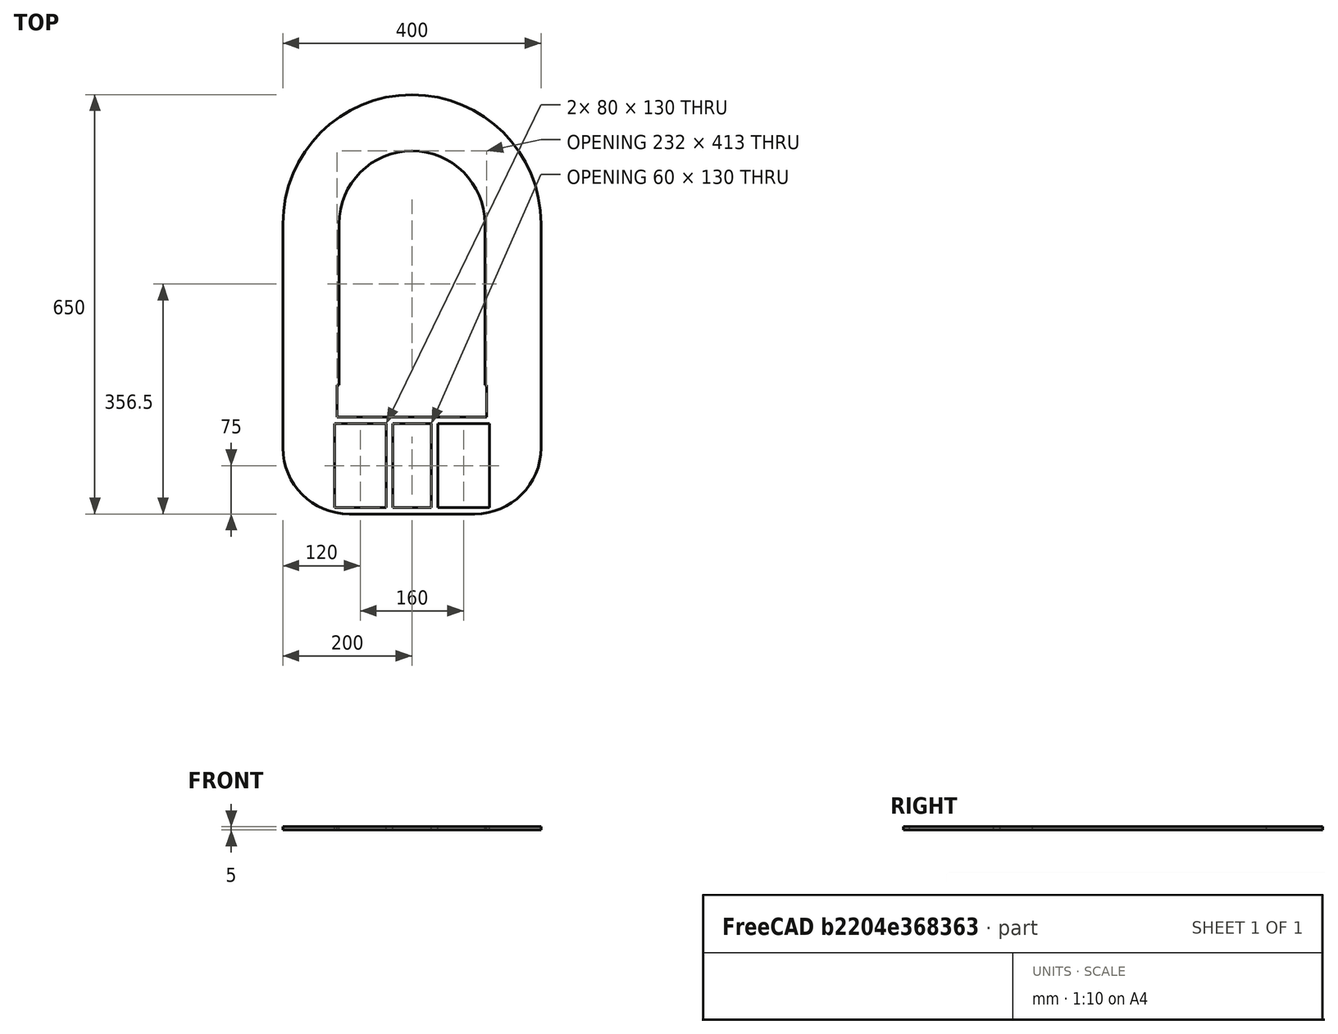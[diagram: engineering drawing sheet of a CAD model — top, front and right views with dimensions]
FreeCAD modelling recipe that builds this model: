
FCSTD DOCUMENT  (FreeCAD 0.16R6706 (Git))
Label: PlateauSuperieur
License: All rights reserved
LicenseURL: http://en.wikipedia.org/wiki/All_rights_reserved
objects: Sketcher::SketchObject×1, PartDesign::Pad×1
note: 3 computed .brp shape members not serialized (recipe doc carries the construction recipe); baked Part::Feature solids carry a one-line shape summary decoded from their .brp

FEATURE [Sketcher::SketchObject] Sketch
  sketch-geometry (32):
    g0: LineSegment StartX=0 StartY=-300 StartZ=0 EndX=116 EndY=-300 EndZ=0
    g1: LineSegment StartX=116 StartY=-300 StartZ=0 EndX=116 EndY=-250 EndZ=0
    g2: LineSegment StartX=116 StartY=-250 StartZ=0 EndX=113 EndY=-250 EndZ=0
    g3: LineSegment StartX=113 StartY=-250 StartZ=0 EndX=113 EndY=-0.000122513 EndZ=0
    g4: ArcOfCircle CenterX=0 CenterY=0 CenterZ=0 NormalX=0 NormalY=0 NormalZ=1 Radius=113 StartAngle=6.28318 EndAngle=7.85398
    g5: ArcOfCircle CenterX=0 CenterY=0 CenterZ=0 NormalX=0 NormalY=0 NormalZ=1 Radius=200 StartAngle=1.2861e-08 EndAngle=1.5708
    g6: LineSegment StartX=200 StartY=2.5722e-06 StartZ=0 EndX=200 EndY=-347.34 EndZ=0
    g7: LineSegment StartX=0 StartY=-450 StartZ=0 EndX=97.34 EndY=-450 EndZ=0
    g8: ArcOfCircle CenterX=97.34 CenterY=-347.34 CenterZ=0 NormalX=0 NormalY=0 NormalZ=1 Radius=102.66 StartAngle=4.71239 EndAngle=6.28319
    g9: LineSegment StartX=40 StartY=-310 StartZ=0 EndX=120 EndY=-310 EndZ=0
    g10: LineSegment StartX=120 StartY=-310 StartZ=0 EndX=120 EndY=-440 EndZ=0
    g11: LineSegment StartX=120 StartY=-440 StartZ=0 EndX=40 EndY=-440 EndZ=0
    g12: LineSegment StartX=40 StartY=-440 StartZ=0 EndX=40 EndY=-310 EndZ=0
    g13: LineSegment StartX=0 StartY=-310 StartZ=0 EndX=30 EndY=-310 EndZ=0
    g14: LineSegment StartX=30 StartY=-310 StartZ=0 EndX=30 EndY=-440 EndZ=0
    g15: LineSegment StartX=30 StartY=-440 StartZ=0 EndX=0 EndY=-440 EndZ=0
    g16: LineSegment StartX=0 StartY=-300 StartZ=0 EndX=-116 EndY=-300 EndZ=0
    g17: LineSegment StartX=-116 StartY=-300 StartZ=0 EndX=-116 EndY=-250 EndZ=0
    g18: LineSegment StartX=-116 StartY=-250 StartZ=0 EndX=-113 EndY=-250 EndZ=0
    g19: LineSegment StartX=0 StartY=-450 StartZ=0 EndX=-97.34 EndY=-450 EndZ=0
    g20: ArcOfCircle CenterX=-97.34 CenterY=-347.34 CenterZ=0 NormalX=0 NormalY=0 NormalZ=1 Radius=102.66 StartAngle=3.14159 EndAngle=4.71239
    g21: LineSegment StartX=-40 StartY=-310 StartZ=0 EndX=-120 EndY=-310 EndZ=0
    g22: LineSegment StartX=-120 StartY=-310 StartZ=0 EndX=-120 EndY=-440 EndZ=0
    g23: LineSegment StartX=-120 StartY=-440 StartZ=0 EndX=-40 EndY=-440 EndZ=0
    g24: LineSegment StartX=-40 StartY=-440 StartZ=0 EndX=-40 EndY=-310 EndZ=0
    g25: LineSegment StartX=0 StartY=-310 StartZ=0 EndX=-30 EndY=-310 EndZ=0
    g26: LineSegment StartX=-30 StartY=-310 StartZ=0 EndX=-30 EndY=-440 EndZ=0
    g27: LineSegment StartX=-30 StartY=-440 StartZ=0 EndX=0 EndY=-440 EndZ=0
    g28: LineSegment StartX=-113 StartY=-250 StartZ=0 EndX=-113 EndY=-0.000122513 EndZ=0
    g29: ArcOfCircle CenterX=0 CenterY=0 CenterZ=0 NormalX=0 NormalY=0 NormalZ=1 Radius=113 StartAngle=1.5708 EndAngle=3.14159
    g30: ArcOfCircle CenterX=0 CenterY=0 CenterZ=0 NormalX=0 NormalY=0 NormalZ=1 Radius=200 StartAngle=1.5708 EndAngle=3.14159
    g31: LineSegment StartX=-200 StartY=2.5722e-06 StartZ=0 EndX=-200 EndY=-347.34 EndZ=0
  constraints (88):
    c: Horizontal(g0)
    c: Vertical(g1)
    c: Horizontal(g2)
    c: Vertical(g3)
    c: Coincident(g1,g0)
    c: Coincident(g1,g2)
    c: Coincident(g2,g3)
    c: PointOnObject(g4,g-2)
    c: Coincident(g4,g3)
    c: DistanceX(g0,g0) = 116
    c: PointOnObject(g0,g-2)
    c: DistanceY(g1,g1) = 50
    c: DistanceY(g0,g4) = 300
    c: Tangent(g4,g3)
    c: Coincident(g4,g-1)
    c: Coincident(g5,g-1)
    c: PointOnObject(g5,g-2)
    c: Vertical(g6)
    c: Coincident(g6,g5)
    c: Tangent(g6,g5)
    c: Horizontal(g7)
    c: Coincident(g7,g8)
    c: Coincident(g8,g6)
    c: Tangent(g6,g8)
    c: Tangent(g7,g8)
    c: PointOnObject(g7,g-2)
    c: DistanceY(g7,g0) = 150
    c: PointOnObject(g4,g-2)
    c: Coincident(g9,g10)
    c: Coincident(g10,g11)
    c: Coincident(g11,g12)
    c: Coincident(g12,g9)
    c: Horizontal(g9)
    c: Horizontal(g11)
    c: Vertical(g10)
    c: Vertical(g12)
    c: Horizontal(g13)
    c: Coincident(g13,g14)
    c: Vertical(g14)
    c: Coincident(g14,g15)
    c: Horizontal(g15)
    c: PointOnObject(g13,g-2)
    c: PointOnObject(g15,g-2)
    c: Radius(g8) = 102.66
    c: Radius(g4) = 113
    c: Radius(g5) = 200
    c: DistanceX(g15,g15) = 30
    c: DistanceX(g11,g11) = 80
    c: DistanceX(g14,g11) = 10
    c: DistanceY(g13,g0) = 10
    c: PointOnObject(g11,g15)
    c: PointOnObject(g9,g13)
    c: DistanceY(g10,g10) = 130
    c: Horizontal(g16)
    c: Vertical(g17)
    c: Horizontal(g18)
    c: Vertical(g28)
    c: Coincident(g17,g16)
    c: Coincident(g17,g18)
    c: Coincident(g18,g28)
    c: Coincident(g29,g28)
    c: Tangent(g29,g28)
    c: Vertical(g31)
    c: Coincident(g31,g30)
    c: Tangent(g31,g30)
    c: Horizontal(g19)
    c: Coincident(g19,g20)
    c: Coincident(g20,g31)
    c: Tangent(g31,g20)
    c: Tangent(g19,g20)
    c: Coincident(g21,g22)
    c: Coincident(g22,g23)
    c: Coincident(g23,g24)
    c: Coincident(g24,g21)
    c: Horizontal(g21)
    c: Horizontal(g23)
    c: Vertical(g22)
    c: Vertical(g24)
    c: Horizontal(g25)
    c: Coincident(g25,g26)
    c: Vertical(g26)
    c: Coincident(g26,g27)
    c: Horizontal(g27)
    c: Radius(g20) = 102.66
    c: Radius(g29) = 113
    c: Radius(g30) = 200
    c: PointOnObject(g23,g27)
    c: PointOnObject(g21,g25)
FEATURE [PartDesign::Pad] Pad
  Length = 5
  Length2 = 100
  Sketch = -> Sketch
  Type = 0
